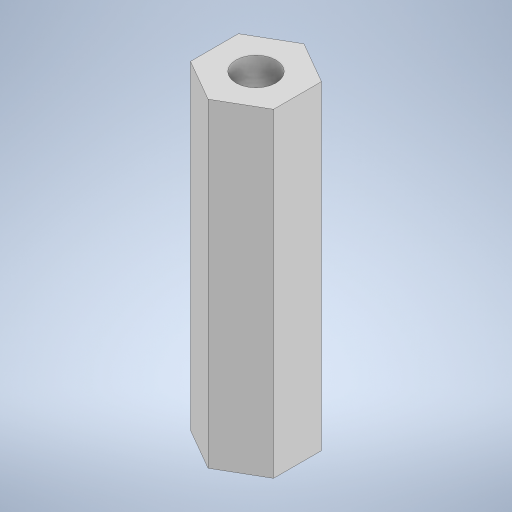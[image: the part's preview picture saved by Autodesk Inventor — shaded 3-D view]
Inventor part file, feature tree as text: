
AUTODESK INVENTOR PART (.ipt)
format: ipt  version: 2023 (Build 270158000, 158)  size: 218,112 bytes
history: native  units: in
note: dims shown in document units (in); Inventor stores cm internally (conversion verified against a paired STEP export)
features: extrude x1, sketch x1
ambient origin geometry x8: Origin, YZ Plane, XZ Plane, XY Plane, X Axis, Y Axis, Z Axis, Center Point
bodies: Solid1 (feature_tree)
feature tree (2):
  extrude  "Extrusion1"  Depth=0.7874in TaperAngle=0.0deg
  sketch  "Sketch1"  dims[d0=0.0984in d2=0.7874in d3=0.0in]
